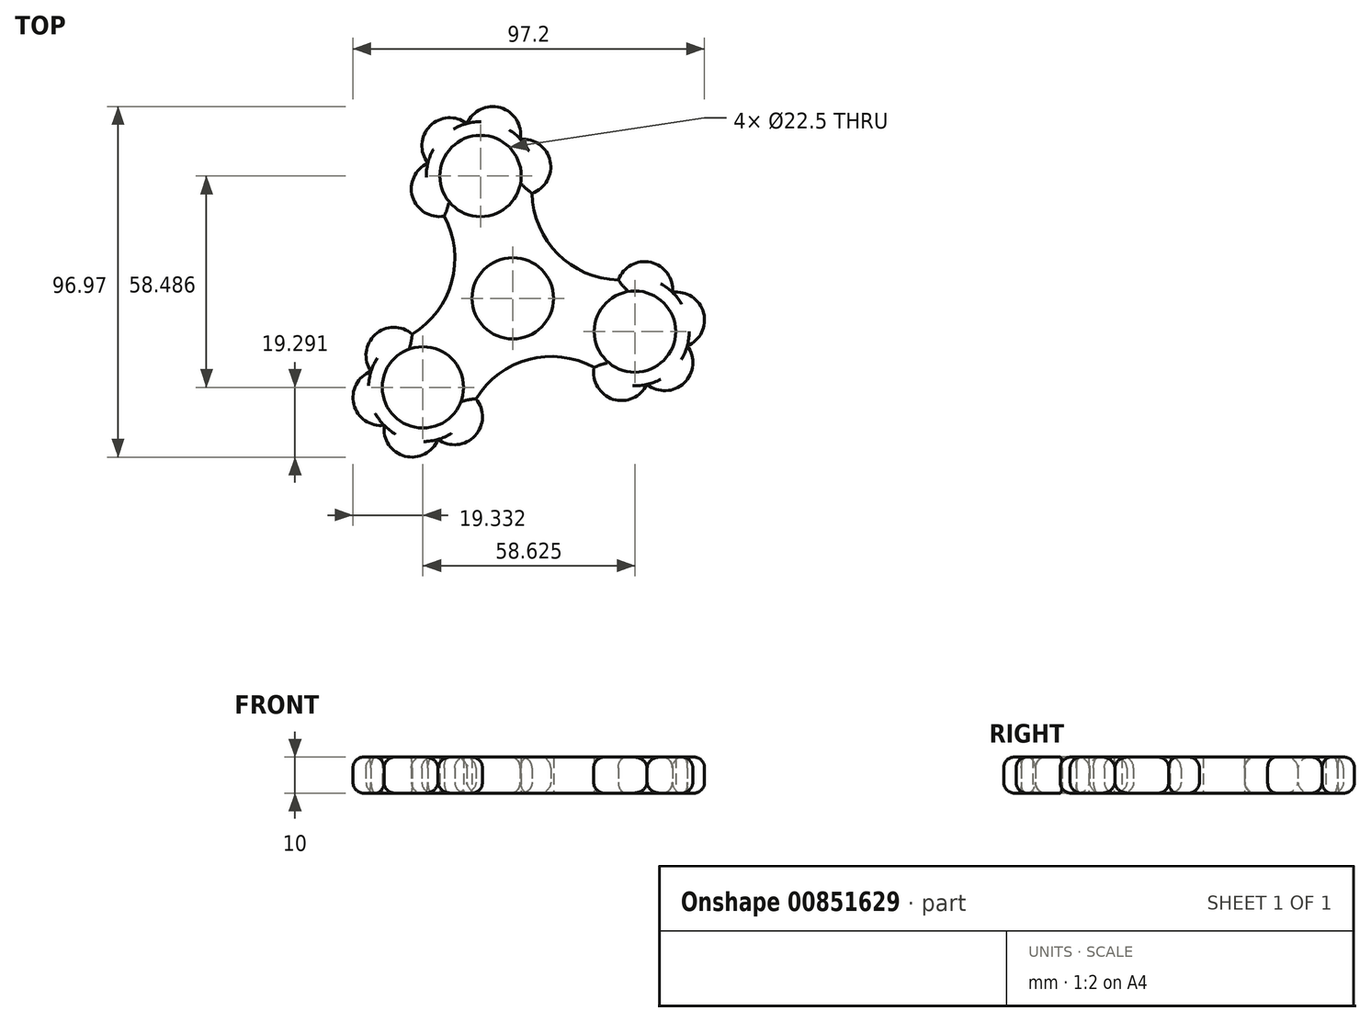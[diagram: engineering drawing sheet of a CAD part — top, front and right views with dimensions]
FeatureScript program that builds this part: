
annotation { "Feature Type Name" : "Feature", "Feature Type Description" : "" }
export const myFeature = defineFeature(function(context is Context, id is Id, definition is map)
    precondition{}
    {
        {
            var Q0;
            Q0=qCreatedBy(makeId("Top.planeOp"),FACE);
            var sketch = newSketch(context, id + "F0", { "sketchPlane" : qUnion([Q0])});
            skCircle(sketch, "E0", {"center": v(0, 0) * mm, "radius": 11.25 * mm});
            skLineSegment(sketch, "E1", {"start": v(0, 0) * mm, "end": v(-8.9, 33.85) * mm});
            skCircle(sketch, "E2", {"center": v(-8.9, 33.85) * mm, "radius": 11.25 * mm});
            skCircle(sketch, "E3", {"center": v(0, 0) * mm, "radius": 15 * mm});
            skCircle(sketch, "E4", {"center": v(-8.9, 33.85) * mm, "radius": 15 * mm});
            skCircle(sketch, "E5.1.0", {"center": v(-24.86, -24.64) * mm, "radius": 15 * mm});
            skCircle(sketch, "E5.1.1", {"center": v(-24.86, -24.64) * mm, "radius": 11.25 * mm});
            skLineSegment(sketch, "E5.1.2", {"start": v(0, 0) * mm, "end": v(-24.86, -24.64) * mm});
            skCircle(sketch, "E5.2.0", {"center": v(33.77, -9.2) * mm, "radius": 15 * mm});
            skCircle(sketch, "E5.2.1", {"center": v(33.77, -9.2) * mm, "radius": 11.25 * mm});
            skLineSegment(sketch, "E5.2.2", {"start": v(0, 0) * mm, "end": v(33.77, -9.2) * mm});
            skPoint(sketch, "E6", {"position": v(-18.98, 22.73) * mm});
            skPoint(sketch, "E7.MirrorP", {"position": v(5.33, 29.13) * mm});
            skPoint(sketch, "E8.1.0", {"position": v(-27.9, -9.95) * mm});
            skPoint(sketch, "E8.1.1", {"position": v(-10.2, -27.8) * mm});
            skPoint(sketch, "E8.2.0", {"position": v(22.56, -19.18) * mm});
            skPoint(sketch, "E8.2.1", {"position": v(29.17, 5.07) * mm});
            skArc(sketch, "E9", {"start": v(-27.9, -9.95) * mm, "mid": v(-16.87, 4.6) * mm, "end": v(-18.98, 22.73) * mm});
            skArc(sketch, "E10.1.0", {"start": v(22.56, -19.18) * mm, "mid": v(4.45, -16.9) * mm, "end": v(-10.2, -27.8) * mm});
            skArc(sketch, "E10.2.0", {"start": v(5.33, 29.13) * mm, "mid": v(12.42, 12.3) * mm, "end": v(29.17, 5.07) * mm});
            skCircle(sketch, "E11.1.0", {"center": v(-24.86, -24.64) * mm, "radius": 20 * mm});
            skCircle(sketch, "E11.2.0", {"center": v(33.77, -9.2) * mm, "radius": 20 * mm});
            skLineSegment(sketch, "E12", {"start": v(-8.9, 33.85) * mm, "end": v(-18.98, 22.73) * mm, "construction": true});
            skArc(sketch, "E13", {"start": v(-23.48, 37.4) * mm, "mid": v(-27.72, 28.08) * mm, "end": v(-18.98, 22.73) * mm});
            skArc(sketch, "E14.1.0", {"start": v(-12.7, 48.36) * mm, "mid": v(-22.92, 47.66) * mm, "end": v(-23.47, 37.44) * mm});
            skArc(sketch, "E14.2.0", {"start": v(2.07, 44.07) * mm, "mid": v(-3.4, 52.73) * mm, "end": v(-12.66, 48.37) * mm});
            skArc(sketch, "E15.3.3.0", {"start": v(5.3, 29.03) * mm, "mid": v(10.33, 37.96) * mm, "end": v(2.1, 44.04) * mm});
            skArc(sketch, "E16.1.0", {"start": v(-35.53, -35.17) * mm, "mid": v(-29.82, -43.68) * mm, "end": v(-20.68, -39.05) * mm});
            skArc(sketch, "E16.1.1", {"start": v(-20.65, -39.04) * mm, "mid": v(-10.46, -38.04) * mm, "end": v(-10.2, -27.8) * mm});
            skArc(sketch, "E16.1.2", {"start": v(-39.2, -20.24) * mm, "mid": v(-43.97, -29.3) * mm, "end": v(-35.56, -35.15) * mm});
            skArc(sketch, "E16.1.3", {"start": v(-27.8, -9.93) * mm, "mid": v(-38.04, -10.03) * mm, "end": v(-39.19, -20.2) * mm});
            skArc(sketch, "E16.2.0", {"start": v(48.23, -13.19) * mm, "mid": v(52.74, -3.99) * mm, "end": v(44.16, 1.61) * mm});
            skArc(sketch, "E16.2.1", {"start": v(44.13, 1.63) * mm, "mid": v(38.17, 9.97) * mm, "end": v(29.17, 5.07) * mm});
            skArc(sketch, "E16.2.2", {"start": v(37.13, -23.83) * mm, "mid": v(47.37, -23.43) * mm, "end": v(48.22, -13.22) * mm});
            skArc(sketch, "E16.2.3", {"start": v(22.5, -19.1) * mm, "mid": v(27.7, -27.93) * mm, "end": v(37.1, -23.83) * mm});
            skCircle(sketch, "E17.2.0", {"center": v(-8.9, 33.85) * mm, "radius": 20 * mm});
            skSolve(sketch);
        }
        {
            var Q0;
            {var subQ0=sQuery(id+"F0.wireOp",EDGE,"E16.1.3");var subQ1=sQuery(id+"F0.wireOp",EDGE,"E5.1.0");var subQ2=makeQuery(id+"F0.imprint","INTERSECT",VERTEX,{"disambiguationData":[OD(0.0)],"derivedFrom":[subQ1,subQ0]});Q0=makeQuery(id+"F0.imprint","IMPRINT",FACE,{"disambiguationData":[TD([[makeQuery(id+"F0.imprint","IMPRINT",EDGE,{"disambiguationData":[TD([[subQ2,-1.0]])],"derivedFrom":subQ1}),-1.0]])]});}
            var Q1;
            {var subQ0=sQuery(id+"F0.wireOp",EDGE,"E16.1.2");Q1=makeQuery(id+"F0.imprint","IMPRINT",FACE,{"disambiguationData":[TD([[makeQuery(id+"F0.imprint","IMPRINT",EDGE,{"derivedFrom":subQ0}),1.0]])]});}
            var Q2;
            {var subQ0=sQuery(id+"F0.wireOp",EDGE,"E16.1.0");Q2=makeQuery(id+"F0.imprint","IMPRINT",FACE,{"disambiguationData":[TD([[makeQuery(id+"F0.imprint","IMPRINT",EDGE,{"derivedFrom":subQ0}),1.0]])]});}
            var Q3;
            {var subQ0=sQuery(id+"F0.wireOp",EDGE,"E16.1.1");Q3=makeQuery(id+"F0.imprint","IMPRINT",FACE,{"disambiguationData":[TD([[makeQuery(id+"F0.imprint","IMPRINT",EDGE,{"derivedFrom":subQ0}),1.0]])]});}
            var Q4;
            {var subQ1=sQuery(id+"F0.wireOp",EDGE,"E5.1.0");var subQ3=sQuery(id+"F0.wireOp",EDGE,"E5.1.2");var subQ4=makeQuery(id+"F0.imprint","INTERSECT",VERTEX,{"derivedFrom":[subQ1,subQ3]});Q4=makeQuery(id+"F0.imprint","IMPRINT",FACE,{"disambiguationData":[TD([[makeQuery(id+"F0.imprint","IMPRINT",EDGE,{"disambiguationData":[TD([[subQ4,1.0]])],"derivedFrom":subQ1}),-1.0]])]});}
            var Q5;
            {var subQ5=sQuery(id+"F0.wireOp",EDGE,"E16.1.3");var subQ7=sQuery(id+"F0.wireOp",EDGE,"E5.1.0");var subQ9=makeQuery(id+"F0.imprint","INTERSECT",VERTEX,{"disambiguationData":[OD(0.0)],"derivedFrom":[subQ7,subQ5]});Q5=makeQuery(id+"F0.imprint","IMPRINT",FACE,{"disambiguationData":[TD([[makeQuery(id+"F0.imprint","IMPRINT",EDGE,{"disambiguationData":[TD([[subQ9,1.0]])],"derivedFrom":subQ7}),-1.0]])]});}
            var Q6;
            {var subQ3=sQuery(id+"F0.wireOp",EDGE,"E11.2.0");var subQ5=sQuery(id+"F0.wireOp",EDGE,"E10.1.0");var subQ6=makeQuery(id+"F0.imprint","INTERSECT",VERTEX,{"derivedFrom":[subQ5,subQ3]});Q6=makeQuery(id+"F0.imprint","IMPRINT",FACE,{"disambiguationData":[TD([[makeQuery(id+"F0.imprint","IMPRINT",EDGE,{"disambiguationData":[TD([[subQ6,-1.0]])],"derivedFrom":subQ5}),-1.0]])]});}
            var Q7;
            {var subQ3=sQuery(id+"F0.wireOp",EDGE,"E11.1.0");var subQ5=sQuery(id+"F0.wireOp",EDGE,"E9");var subQ6=makeQuery(id+"F0.imprint","INTERSECT",VERTEX,{"derivedFrom":[subQ5,subQ3]});Q7=makeQuery(id+"F0.imprint","IMPRINT",FACE,{"disambiguationData":[TD([[makeQuery(id+"F0.imprint","IMPRINT",EDGE,{"disambiguationData":[TD([[subQ6,-1.0]])],"derivedFrom":subQ5}),-1.0]])]});}
            var Q8;
            {var subQ0=sQuery(id+"F0.wireOp",EDGE,"E17.2.0");var subQ5=sQuery(id+"F0.wireOp",EDGE,"E10.2.0");var subQ6=makeQuery(id+"F0.imprint","INTERSECT",VERTEX,{"derivedFrom":[subQ5,subQ0]});Q8=makeQuery(id+"F0.imprint","IMPRINT",FACE,{"disambiguationData":[TD([[makeQuery(id+"F0.imprint","IMPRINT",EDGE,{"disambiguationData":[TD([[subQ6,-1.0]])],"derivedFrom":subQ5}),-1.0]])]});}
            var Q9;
            {var subQ0=sQuery(id+"F0.wireOp",EDGE,"E15.3.3.0");var subQ1=sQuery(id+"F0.wireOp",EDGE,"E4");var subQ2=makeQuery(id+"F0.imprint","INTERSECT",VERTEX,{"disambiguationData":[OD(0.0)],"derivedFrom":[subQ1,subQ0]});Q9=makeQuery(id+"F0.imprint","IMPRINT",FACE,{"disambiguationData":[TD([[makeQuery(id+"F0.imprint","IMPRINT",EDGE,{"disambiguationData":[TD([[subQ2,-1.0]])],"derivedFrom":subQ1}),-1.0]])]});}
            var Q10;
            {var subQ0=sQuery(id+"F0.wireOp",EDGE,"E4");var subQ1=sQuery(id+"F0.wireOp",EDGE,"E1");var subQ2=makeQuery(id+"F0.imprint","INTERSECT",VERTEX,{"derivedFrom":[subQ1,subQ0]});Q10=makeQuery(id+"F0.imprint","IMPRINT",FACE,{"disambiguationData":[TD([[makeQuery(id+"F0.imprint","IMPRINT",EDGE,{"disambiguationData":[TD([[subQ2,1.0]])],"derivedFrom":subQ1}),1.0]])]});}
            var Q11;
            {var subQ3=sQuery(id+"F0.wireOp",EDGE,"E15.3.3.0");var subQ5=sQuery(id+"F0.wireOp",EDGE,"E4");var subQ6=makeQuery(id+"F0.imprint","INTERSECT",VERTEX,{"disambiguationData":[OD(0.0)],"derivedFrom":[subQ5,subQ3]});Q11=makeQuery(id+"F0.imprint","IMPRINT",FACE,{"disambiguationData":[TD([[makeQuery(id+"F0.imprint","IMPRINT",EDGE,{"disambiguationData":[TD([[subQ6,1.0]])],"derivedFrom":subQ5}),-1.0]])]});}
            var Q12;
            {var subQ1=sQuery(id+"F0.wireOp",EDGE,"E5.2.0");var subQ3=sQuery(id+"F0.wireOp",EDGE,"E5.2.2");var subQ4=makeQuery(id+"F0.imprint","INTERSECT",VERTEX,{"derivedFrom":[subQ1,subQ3]});Q12=makeQuery(id+"F0.imprint","IMPRINT",FACE,{"disambiguationData":[TD([[makeQuery(id+"F0.imprint","IMPRINT",EDGE,{"disambiguationData":[TD([[subQ4,1.0]])],"derivedFrom":subQ1}),-1.0]])]});}
            var Q13;
            {var subQ0=sQuery(id+"F0.wireOp",EDGE,"E16.2.3");var subQ1=sQuery(id+"F0.wireOp",EDGE,"E5.2.0");var subQ2=makeQuery(id+"F0.imprint","INTERSECT",VERTEX,{"disambiguationData":[OD(0.0)],"derivedFrom":[subQ1,subQ0]});Q13=makeQuery(id+"F0.imprint","IMPRINT",FACE,{"disambiguationData":[TD([[makeQuery(id+"F0.imprint","IMPRINT",EDGE,{"disambiguationData":[TD([[subQ2,1.0]])],"derivedFrom":subQ1}),-1.0]])]});}
            var Q14;
            {var subQ0=sQuery(id+"F0.wireOp",EDGE,"E16.2.3");var subQ1=sQuery(id+"F0.wireOp",EDGE,"E5.2.0");var subQ2=makeQuery(id+"F0.imprint","INTERSECT",VERTEX,{"disambiguationData":[OD(0.0)],"derivedFrom":[subQ1,subQ0]});Q14=makeQuery(id+"F0.imprint","IMPRINT",FACE,{"disambiguationData":[TD([[makeQuery(id+"F0.imprint","IMPRINT",EDGE,{"disambiguationData":[TD([[subQ2,-1.0]])],"derivedFrom":subQ1}),-1.0]])]});}
            var Q15;
            {var subQ0=sQuery(id+"F0.wireOp",EDGE,"E16.2.2");Q15=makeQuery(id+"F0.imprint","IMPRINT",FACE,{"disambiguationData":[TD([[makeQuery(id+"F0.imprint","IMPRINT",EDGE,{"derivedFrom":subQ0}),1.0]])]});}
            var Q16;
            {var subQ0=sQuery(id+"F0.wireOp",EDGE,"E16.2.0");Q16=makeQuery(id+"F0.imprint","IMPRINT",FACE,{"disambiguationData":[TD([[makeQuery(id+"F0.imprint","IMPRINT",EDGE,{"derivedFrom":subQ0}),1.0]])]});}
            var Q17;
            {var subQ0=sQuery(id+"F0.wireOp",EDGE,"E16.2.1");Q17=makeQuery(id+"F0.imprint","IMPRINT",FACE,{"disambiguationData":[TD([[makeQuery(id+"F0.imprint","IMPRINT",EDGE,{"derivedFrom":subQ0}),1.0]])]});}
            var Q18;
            {var subQ0=sQuery(id+"F0.wireOp",EDGE,"E14.2.0");Q18=makeQuery(id+"F0.imprint","IMPRINT",FACE,{"disambiguationData":[TD([[makeQuery(id+"F0.imprint","IMPRINT",EDGE,{"derivedFrom":subQ0}),1.0]])]});}
            var Q19;
            {var subQ0=sQuery(id+"F0.wireOp",EDGE,"E14.1.0");Q19=makeQuery(id+"F0.imprint","IMPRINT",FACE,{"disambiguationData":[TD([[makeQuery(id+"F0.imprint","IMPRINT",EDGE,{"derivedFrom":subQ0}),1.0]])]});}
            var Q20;
            {var subQ0=sQuery(id+"F0.wireOp",EDGE,"E13");Q20=makeQuery(id+"F0.imprint","IMPRINT",FACE,{"disambiguationData":[TD([[makeQuery(id+"F0.imprint","IMPRINT",EDGE,{"derivedFrom":subQ0}),1.0]])]});}
            var Q21;
            Q21=makeQuery(id+"F0.imprint","IMPRINT",FACE,{"disambiguationData":[TD([[makeQuery(id+"F0.imprint","IMPRINT",EDGE,{"derivedFrom":sQuery(id+"F0.wireOp",EDGE,"E5.2.1")}),-1.0]])]});
            var Q22;
            Q22=makeQuery(id+"F0.imprint","IMPRINT",FACE,{"disambiguationData":[TD([[makeQuery(id+"F0.imprint","IMPRINT",EDGE,{"derivedFrom":sQuery(id+"F0.wireOp",EDGE,"E5.1.1")}),-1.0]])]});
            var Q23;
            Q23=makeQuery(id+"F0.imprint","IMPRINT",FACE,{"disambiguationData":[TD([[makeQuery(id+"F0.imprint","IMPRINT",EDGE,{"derivedFrom":sQuery(id+"F0.wireOp",EDGE,"E2")}),-1.0]])]});
            var Q24;
            {var subQ0=sQuery(id+"F0.wireOp",EDGE,"E1");var subQ1=sQuery(id+"F0.wireOp",EDGE,"E0");var subQ2=makeQuery(id+"F0.imprint","INTERSECT",VERTEX,{"derivedFrom":[subQ1,subQ0]});Q24=makeQuery(id+"F0.imprint","IMPRINT",FACE,{"disambiguationData":[TD([[makeQuery(id+"F0.imprint","IMPRINT",EDGE,{"disambiguationData":[TD([[subQ2,1.0]])],"derivedFrom":subQ1}),-1.0]])]});}
            var Q25;
            {var subQ0=sQuery(id+"F0.wireOp",EDGE,"E5.1.2");var subQ1=sQuery(id+"F0.wireOp",EDGE,"E0");var subQ2=makeQuery(id+"F0.imprint","INTERSECT",VERTEX,{"derivedFrom":[subQ1,subQ0]});Q25=makeQuery(id+"F0.imprint","IMPRINT",FACE,{"disambiguationData":[TD([[makeQuery(id+"F0.imprint","IMPRINT",EDGE,{"disambiguationData":[TD([[subQ2,1.0]])],"derivedFrom":subQ1}),-1.0]])]});}
            var Q26;
            {var subQ0=sQuery(id+"F0.wireOp",EDGE,"E5.1.2");var subQ1=sQuery(id+"F0.wireOp",EDGE,"E0");var subQ2=makeQuery(id+"F0.imprint","INTERSECT",VERTEX,{"derivedFrom":[subQ1,subQ0]});Q26=makeQuery(id+"F0.imprint","IMPRINT",FACE,{"disambiguationData":[TD([[makeQuery(id+"F0.imprint","IMPRINT",EDGE,{"disambiguationData":[TD([[subQ2,-1.0]])],"derivedFrom":subQ1}),-1.0]])]});}
            extrude(context, id + "F1", {"entities" : qUnion([Q0, Q1, Q2, Q3, Q4, Q5, Q6, Q7, Q8, Q9, Q10, Q11, Q12, Q13, Q14, Q15, Q16, Q17, Q18, Q19, Q20, Q21, Q22, Q23, Q24, Q25, Q26]), "depth" : 10 * mm, "offsetDistance" : 25 * mm});
        }
        {
            var Q0;
            Q0=makeQuery(id+"F1.opExtrude","CAP_EDGE",EDGE,{"disambiguationData":[OSD([sQuery(id+"F0.wireOp",EDGE,"E14.1.0")])],"isStart":false});
            var Q1;
            Q1=makeQuery(id+"F1.opExtrude","CAP_EDGE",EDGE,{"disambiguationData":[OSD([sQuery(id+"F0.wireOp",EDGE,"E14.1.0")])],"isStart":true});
            var Q2;
            Q2=makeQuery(id+"F1.opExtrude","CAP_EDGE",EDGE,{"disambiguationData":[OSD([sQuery(id+"F0.wireOp",EDGE,"E14.2.0")])],"isStart":true});
            var Q3;
            Q3=makeQuery(id+"F1.opExtrude","CAP_EDGE",EDGE,{"disambiguationData":[OSD([sQuery(id+"F0.wireOp",EDGE,"E14.2.0")])],"isStart":false});
            var Q4;
            Q4=makeQuery(id+"F1.opExtrude","CAP_EDGE",EDGE,{"disambiguationData":[OSD([sQuery(id+"F0.wireOp",EDGE,"E15.3.3.0")])],"isStart":true});
            var Q5;
            Q5=makeQuery(id+"F1.opExtrude","CAP_EDGE",EDGE,{"disambiguationData":[OSD([sQuery(id+"F0.wireOp",EDGE,"E15.3.3.0")])],"isStart":false});
            var Q6;
            Q6=makeQuery(id+"F1.opExtrude","CAP_EDGE",EDGE,{"disambiguationData":[OSD([sQuery(id+"F0.wireOp",EDGE,"E10.2.0")])],"isStart":false});
            var Q7;
            Q7=makeQuery(id+"F1.opExtrude","CAP_EDGE",EDGE,{"disambiguationData":[OSD([sQuery(id+"F0.wireOp",EDGE,"E10.2.0")])],"isStart":true});
            var Q8;
            Q8=makeQuery(id+"F1.opExtrude","CAP_EDGE",EDGE,{"disambiguationData":[OSD([sQuery(id+"F0.wireOp",EDGE,"E16.2.1")])],"isStart":true});
            var Q9;
            Q9=makeQuery(id+"F1.opExtrude","CAP_EDGE",EDGE,{"disambiguationData":[OSD([sQuery(id+"F0.wireOp",EDGE,"E16.2.1")])],"isStart":false});
            var Q10;
            Q10=makeQuery(id+"F1.opExtrude","CAP_EDGE",EDGE,{"disambiguationData":[OSD([sQuery(id+"F0.wireOp",EDGE,"E16.2.0")])],"isStart":false});
            var Q11;
            Q11=makeQuery(id+"F1.opExtrude","CAP_EDGE",EDGE,{"disambiguationData":[OSD([sQuery(id+"F0.wireOp",EDGE,"E16.2.0")])],"isStart":true});
            var Q12;
            Q12=makeQuery(id+"F1.opExtrude","CAP_EDGE",EDGE,{"disambiguationData":[OSD([sQuery(id+"F0.wireOp",EDGE,"E16.2.2")])],"isStart":true});
            var Q13;
            Q13=makeQuery(id+"F1.opExtrude","CAP_EDGE",EDGE,{"disambiguationData":[OSD([sQuery(id+"F0.wireOp",EDGE,"E16.2.3")])],"isStart":true});
            var Q14;
            Q14=makeQuery(id+"F1.opExtrude","CAP_EDGE",EDGE,{"disambiguationData":[OSD([sQuery(id+"F0.wireOp",EDGE,"E16.2.2")])],"isStart":false});
            var Q15;
            Q15=makeQuery(id+"F1.opExtrude","CAP_EDGE",EDGE,{"disambiguationData":[OSD([sQuery(id+"F0.wireOp",EDGE,"E16.2.3")])],"isStart":false});
            var Q16;
            Q16=makeQuery(id+"F1.opExtrude","CAP_EDGE",EDGE,{"disambiguationData":[OSD([sQuery(id+"F0.wireOp",EDGE,"E10.1.0")])],"isStart":false});
            var Q17;
            Q17=makeQuery(id+"F1.opExtrude","CAP_EDGE",EDGE,{"disambiguationData":[OSD([sQuery(id+"F0.wireOp",EDGE,"E10.1.0")])],"isStart":true});
            var Q18;
            Q18=makeQuery(id+"F1.opExtrude","CAP_EDGE",EDGE,{"disambiguationData":[OSD([sQuery(id+"F0.wireOp",EDGE,"E16.1.1")])],"isStart":false});
            var Q19;
            Q19=makeQuery(id+"F1.opExtrude","CAP_EDGE",EDGE,{"disambiguationData":[OSD([sQuery(id+"F0.wireOp",EDGE,"E9")])],"isStart":false});
            var Q20;
            Q20=makeQuery(id+"F1.opExtrude","CAP_EDGE",EDGE,{"disambiguationData":[OSD([sQuery(id+"F0.wireOp",EDGE,"E9")])],"isStart":true});
            var Q21;
            Q21=makeQuery(id+"F1.opExtrude","CAP_EDGE",EDGE,{"disambiguationData":[OSD([sQuery(id+"F0.wireOp",EDGE,"E16.1.0")])],"isStart":false});
            var Q22;
            Q22=makeQuery(id+"F1.opExtrude","CAP_EDGE",EDGE,{"disambiguationData":[OSD([sQuery(id+"F0.wireOp",EDGE,"E16.1.2")])],"isStart":false});
            var Q23;
            Q23=makeQuery(id+"F1.opExtrude","CAP_EDGE",EDGE,{"disambiguationData":[OSD([sQuery(id+"F0.wireOp",EDGE,"E16.1.3")])],"isStart":false});
            var Q24;
            Q24=makeQuery(id+"F1.opExtrude","CAP_EDGE",EDGE,{"disambiguationData":[OSD([sQuery(id+"F0.wireOp",EDGE,"E16.1.1")])],"isStart":true});
            var Q25;
            Q25=makeQuery(id+"F1.opExtrude","CAP_EDGE",EDGE,{"disambiguationData":[OSD([sQuery(id+"F0.wireOp",EDGE,"E16.1.0")])],"isStart":true});
            var Q26;
            Q26=makeQuery(id+"F1.opExtrude","CAP_EDGE",EDGE,{"disambiguationData":[OSD([sQuery(id+"F0.wireOp",EDGE,"E16.1.2")])],"isStart":true});
            var Q27;
            Q27=makeQuery(id+"F1.opExtrude","CAP_EDGE",EDGE,{"disambiguationData":[OSD([sQuery(id+"F0.wireOp",EDGE,"E13")])],"isStart":true});
            var Q28;
            Q28=makeQuery(id+"F1.opExtrude","CAP_EDGE",EDGE,{"disambiguationData":[OSD([sQuery(id+"F0.wireOp",EDGE,"E13")])],"isStart":false});
            var Q29;
            Q29=makeQuery(id+"F1.opExtrude","CAP_EDGE",EDGE,{"disambiguationData":[OSD([sQuery(id+"F0.wireOp",EDGE,"E16.1.3")])],"isStart":true});
            fillet(context, id + "F2", {"entities" : qUnion([Q0, Q1, Q2, Q3, Q4, Q5, Q6, Q7, Q8, Q9, Q10, Q11, Q12, Q13, Q14, Q15, Q16, Q17, Q18, Q19, Q20, Q21, Q22, Q23, Q24, Q25, Q26, Q27, Q28, Q29]), "radius" : 3 * mm, "tangentPropagation" : true, "allowEdgeOverflow" : false});
        }
    });
